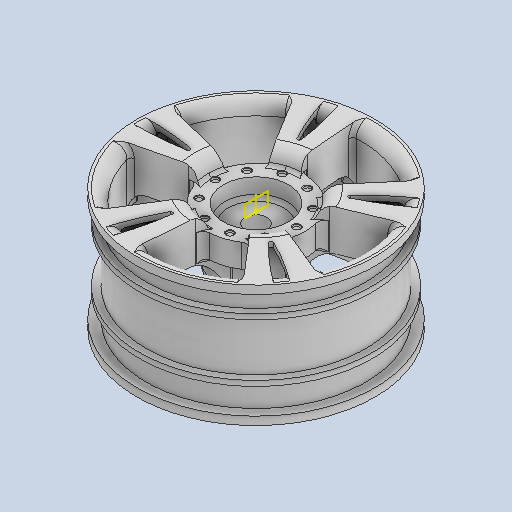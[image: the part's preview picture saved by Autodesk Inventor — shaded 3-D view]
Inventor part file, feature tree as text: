
AUTODESK INVENTOR PART (.ipt)
format: ipt  version: 2024 (Build 280153000, 153)  size: 1,590,784 bytes
history: native  units: in
note: dims shown in document units (in); Inventor stores cm internally (conversion verified against a paired STEP export)
features: sketch x16, fillet x11, extrude x7, revolve x6, projected_geometry x6, other x4, pattern_circular x3, plane x2, hole x1, direct_edit x1
ambient origin geometry x8: Origin, YZ Plane, XZ Plane, XY Plane, X Axis, Y Axis, Z Axis, Center Point
bodies: Solid1 (feature_tree)
feature tree (57):
  revolve  "Revolution1"  [1 undecoded]
  sketch  "Sketch2"  dims[d2=90.0deg d3=0.0805in]
  sketch  "Sketch3"  dims[d4=0.07in d5=0.07in]
  revolve  "Revolution2"  [1 undecoded]
  revolve  "Revolution3"  [1 undecoded]
  extrude  "Extrusion1"  Depth=0.275in
  extrude  "Extrusion2"  Depth=0.275in
  extrude  "Extrusion3"  TaperAngle=90.0deg  [1 undecoded]
  fillet  "Fillet1"  Radius=1.8in
  extrude  "Extrusion4"  Depth=0.66in
  fillet  "Fillet2"  Radius=1.8in
  pattern_circular  "Circular Pattern1"  [2 undecoded]
  revolve  "Revolution4"  [1 undecoded]
  revolve  "Revolution5"  [1 undecoded]
  fillet  "Fillet3"  [1 undecoded]
  other  "Work Point1"
  plane  "Work Plane1"
  revolve  "Revolution6"  [1 undecoded]
  fillet  "Fillet4"  [1 undecoded]
  fillet  "Fillet5"  Radius=0.5841in
  fillet  "Fillet6"  Radius=0.063in
  extrude  "Extrusion5"  Depth=0.3937in
  fillet  "Fillet7"  [1 undecoded]
  extrude  "Extrusion6"  Depth=0.3937in
  pattern_circular  "Circular Pattern2"  [2 undecoded]
  plane  "Work Plane2"
  extrude  "Extrusion7"  Depth=0.3937in
  hole  "Hole1"  [1 undecoded]
  fillet  "Fillet8"  Radius=0.1407in
  pattern_circular  "Circular Pattern3"  Angle=90.0deg  [1 undecoded]
  fillet  "Fillet9"  Radius=0.0625in
  fillet  "Fillet10"  Radius=0.032in
  fillet  "Fillet11"  Radius=0.032in
  direct_edit  "Direct Edit1"
  sketch  "Sketch1"  dims[d0=2.045in d1=1.045in]
  sketch  "Sketch4"  dims[d6=90.0deg d7=0.275in]
  sketch  "Sketch5"  dims[d8=0.045in d9=0.275in]
  sketch  "Sketch6"  dims[d10=2.0in d11=90.0deg d12=1.8in]
  sketch  "Sketch7"  dims[d13=0.465in d14=0.0in d15=0.66in d16=1.8in]
  sketch  "Sketch8"  dims[d17=0.465in d18=0.0in]
  sketch  "Sketch9"  dims[d19=0.265in d20=0.0in]
  sketch  "Sketch10"  dims[d21=0.1in]
  sketch  "Sketch11"  dims[d22=0.1855in]
  other  "Work Point2"
  other  "Work Point3"
  sketch  "Sketch12"  dims[d23=0.1875in]
  sketch  "Sketch13"  dims[d24=0.5898in]
  sketch  "Sketch14"  dims[d25=2.25in]
  sketch  "Sketch15"  dims[d26=0.5in]
  sketch  "Sketch16"  dims[d27=0.1in d28=0.35in d29=0.0in d30=0.0156in d31=1.9685in d32=360.0deg d34=0.05in d35=90.0deg d36=0.5841in d37=0.063in d38=0.125in d39=90.0deg d40=0.2in d41=0.1539in d42=0.2009in d43=0.05in d44=0.1407in d45=90.0deg d46=0.0625in d47=0.032in d48=0.032in d49=0.475in d50=0.2in d51=0.0in d52=0.125in d53=0.0721in d54=0.0721in d55=0.05in d56=0.05in d57=0.5375in d58=1.0in d59=0.0in d60=1.9685in d61=360.0deg d63=-0.015in d64=0.7in d65=0.05in d66=0.129in d67=0.1374in d68=0.1875in d69=0.75in d70=0.375in d71=0.25in d72=0.5635in d73=1.0in d74=0.8108in d75=0.005in d76=3.937in d77=360.0deg d79=0.032in d80=0.032in d81=0.032in d82=3.937in d83=0.3937in d84=0.3937in]
  projected_geometry  "Project Cut Edges1"
  projected_geometry  "Project Cut Edges2"
  projected_geometry  "Project Cut Edges3"
  projected_geometry  "Project Cut Edges4"
  projected_geometry  "Project Cut Edges5"
  projected_geometry  "Project Cut Edges6"
  other  "Scale1"
note: 16 required parameter values undecoded (feature->parameter linkage not recoverable at this tier; creation-order binding heuristic only, values carry confidence <= 0.55)